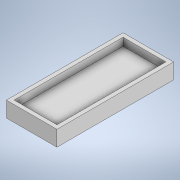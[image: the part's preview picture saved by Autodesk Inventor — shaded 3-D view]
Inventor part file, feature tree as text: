
AUTODESK INVENTOR PART (.ipt)
format: ipt  version: 2021 (Build 250183000, 183)  size: 114,176 bytes
history: native  units: in
note: dims shown in document units (in); Inventor stores cm internally (conversion verified against a paired STEP export)
features: extrude x2, sketch x2, projected_geometry x1
ambient origin geometry x8: Origin, YZ Plane, XZ Plane, XY Plane, X Axis, Y Axis, Z Axis, Center Point
bodies: Solid1 (feature_tree)
feature tree (5):
  extrude  "Extrusion1"  Depth=0.5118in
  extrude  "Extrusion2"  Depth=0.0787in TaperAngle=0.0deg
  sketch  "Sketch1"  dims[d0=1.1811in d1=0.5118in]
  sketch  "Sketch2"  dims[d2=0.0787in d3=0.0in d8=0.0787in d9=0.0in d13=0.0394in d14=0.0394in d15=0.4331in d16=1.1024in]
  projected_geometry  "Projected Loop1"
